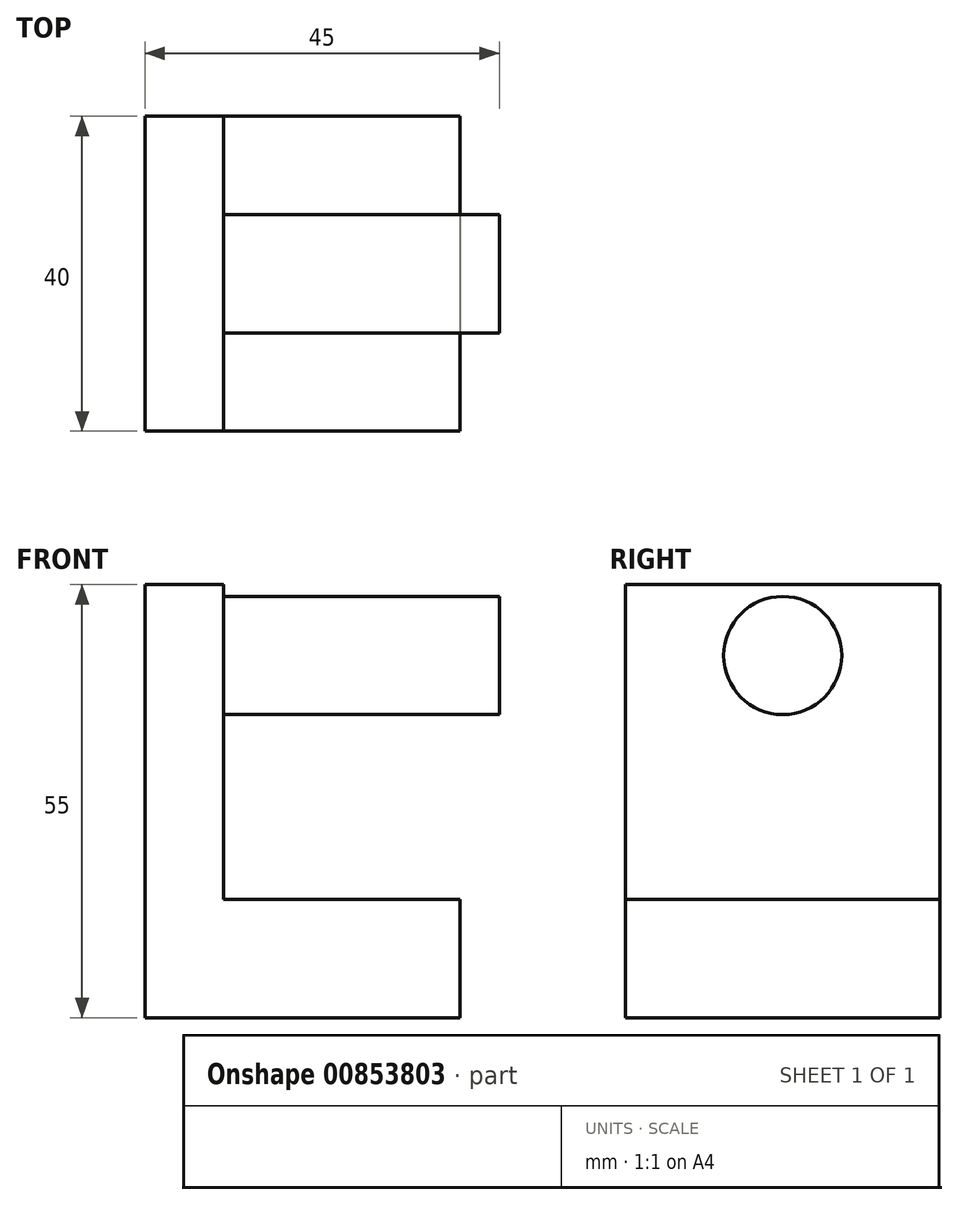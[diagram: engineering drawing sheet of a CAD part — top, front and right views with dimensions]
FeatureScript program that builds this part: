
annotation { "Feature Type Name" : "Feature", "Feature Type Description" : "" }
export const myFeature = defineFeature(function(context is Context, id is Id, definition is map)
    precondition{}
    {
        {
            var Q0;
            Q0=qCreatedBy(makeId("Top.planeOp"),FACE);
            var sketch = newSketch(context, id + "F0", { "sketchPlane" : qUnion([Q0])});
            skLineSegment(sketch, "E0.bottom", {"start": v(20, 20) * mm, "end": v(-20, 20) * mm});
            skLineSegment(sketch, "E0.top", {"start": v(20, -20) * mm, "end": v(-20, -20) * mm});
            skLineSegment(sketch, "E0.left", {"start": v(20, 20) * mm, "end": v(20, -20) * mm});
            skLineSegment(sketch, "E0.right", {"start": v(-20, 20) * mm, "end": v(-20, -20) * mm});
            skPoint(sketch, "E0.middle", {"position": v(0, 0) * mm});
            skLineSegment(sketch, "E1", {"start": v(-10, 20) * mm, "end": v(-10, -20) * mm});
            skSolve(sketch);
        }
        {
            var Q0;
            {var subQ0=sQuery(id+"F0.wireOp",EDGE,"E0.left");Q0=makeQuery(id+"F0.imprint","IMPRINT",FACE,{"disambiguationData":[TD([[makeQuery(id+"F0.imprint","IMPRINT",EDGE,{"derivedFrom":subQ0}),-1.0]])]});}
            extrude(context, id + "F1", {"entities" : qUnion([Q0]), "depth" : 15 * mm, "offsetDistance" : 25 * mm});
        }
        {
            var Q0;
            {var subQ0=sQuery(id+"F0.wireOp",EDGE,"E0.right");Q0=makeQuery(id+"F0.imprint","IMPRINT",FACE,{"disambiguationData":[TD([[makeQuery(id+"F0.imprint","IMPRINT",EDGE,{"derivedFrom":subQ0}),1.0]])]});}
            extrude(context, id + "F2", {"entities" : qUnion([Q0]), "operationType" : NewBodyOperationType.ADD, "depth" : 55 * mm, "offsetDistance" : 25 * mm});
        }
        {
            var Q0;
            Q0=makeQuery(id+"F2.opExtrude","SWEPT_FACE",FACE,{"disambiguationData":[OSD([sQuery(id+"F0.wireOp",EDGE,"E1")])]});
            var sketch = newSketch(context, id + "F3", { "sketchPlane" : qUnion([Q0])});
            skCircle(sketch, "E2", {"center": v(0, 46) * mm, "radius": 7.5 * mm});
            skPoint(sketch, "E2.centerSnap0", {"position": v(0, 55) * mm});
            skSolve(sketch);
        }
        {
            var Q0;
            Q0=makeQuery(id+"F3.imprint","IMPRINT",FACE,{"disambiguationData":[TD([[makeQuery(id+"F3.imprint","IMPRINT",EDGE,{"derivedFrom":sQuery(id+"F3.wireOp",EDGE,"E2")}),1.0]])]});
            extrude(context, id + "F4", {"entities" : qUnion([Q0]), "operationType" : NewBodyOperationType.ADD, "depth" : 35 * mm, "offsetDistance" : 25 * mm});
        }
    });
